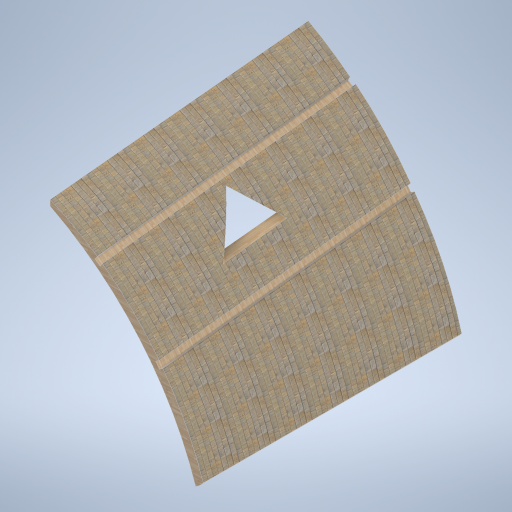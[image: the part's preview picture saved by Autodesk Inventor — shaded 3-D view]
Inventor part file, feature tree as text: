
AUTODESK INVENTOR PART (.ipt)
format: ipt  version: 2024.2 (Build 282272000, 272)  size: 532,480 bytes
history: native  units: mm
features: sketch x3, plane x3, loft x1, extrude x1
ambient origin geometry x8: Origin, YZ Plane, XZ Plane, XY Plane, X Axis, Y Axis, Z Axis, Center Point
bodies: Solid1 (feature_tree)
feature tree (8):
  sketch  "Sketch1"  dims[d5=0.0mm d6=-7900.0mm d7=800.0mm]
  plane  "Work Plane2"
  loft  "Loft1"
  plane  "Work Plane3"
  extrude  "Extrusion1"  Depth=9000.0mm
  plane  "Work Plane1"
  sketch  "Sketch2"  dims[d8=9000.0mm d9=9000.0mm]
  sketch  "Sketch3"  dims[d10=9000.0mm d11=9000.0mm d12=800.0mm d13=0.0mm d14=90.0deg d15=0.0mm d16=90.0deg d17=2500.0mm d18=0.0mm d19=0.0mm]
